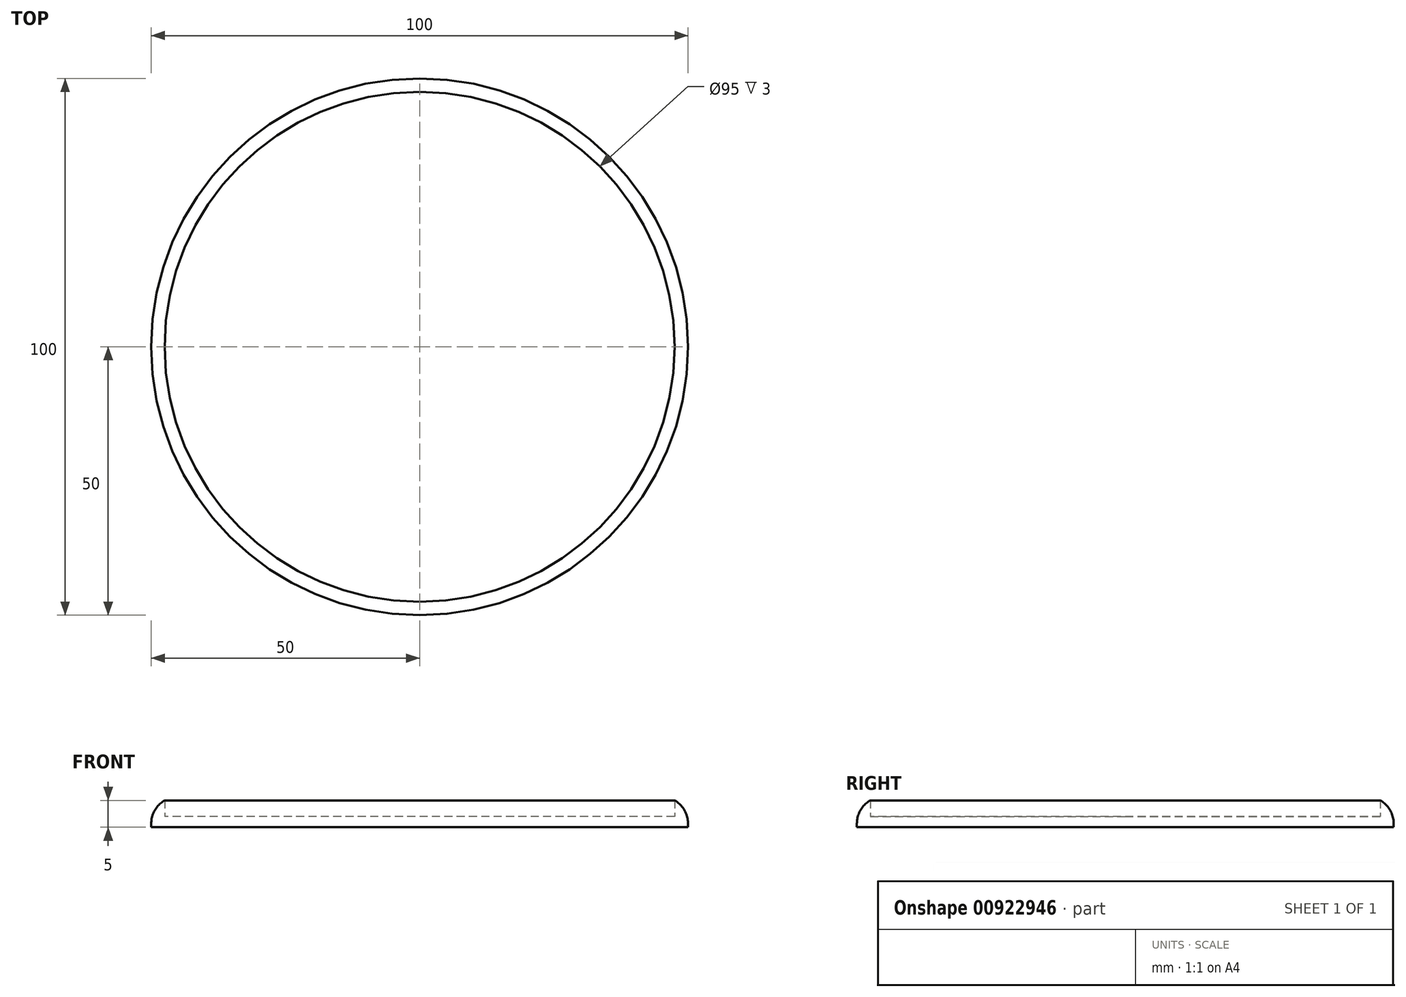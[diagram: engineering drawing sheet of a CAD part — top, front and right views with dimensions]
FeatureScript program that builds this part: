
annotation { "Feature Type Name" : "Feature", "Feature Type Description" : "" }
export const myFeature = defineFeature(function(context is Context, id is Id, definition is map)
    precondition{}
    {
        {
            var Q0;
            Q0=qCreatedBy(makeId("Top.planeOp"),FACE);
            var sketch = newSketch(context, id + "F0", { "sketchPlane" : qUnion([Q0])});
            skCircle(sketch, "E0", {"center": v(0, 0) * mm, "radius": 50 * mm});
            skCircle(sketch, "E1", {"center": v(0, 0) * mm, "radius": 47.5 * mm});
            skSolve(sketch);
        }
        {
            var Q0;
            Q0 = qSketchRegion(id + "F0", true);
            extrude(context, id + "F1", {"entities" : qUnion([Q0]), "depth" : 5 * mm, "offsetDistance" : 25 * mm});
        }
        {
            var Q0;
            Q0=makeQuery(id+"F1.opExtrude","CAP_EDGE",EDGE,{"disambiguationData":[OSD([sQuery(id+"F0.wireOp",EDGE,"E0")])],"isStart":false});
            fillet(context, id + "F2", {"entities" : qUnion([Q0]), "radius" : 5 * mm, "tangentPropagation" : true, "allowEdgeOverflow" : false});
        }
        {
            var Q0;
            Q0=makeQuery(id+"F0.imprint","IMPRINT",FACE,{"disambiguationData":[TD([[makeQuery(id+"F0.imprint","IMPRINT",EDGE,{"derivedFrom":sQuery(id+"F0.wireOp",EDGE,"E1")}),1.0]])]});
            extrude(context, id + "F3", {"entities" : qUnion([Q0]), "operationType" : NewBodyOperationType.ADD, "depth" : 2 * mm, "offsetDistance" : 25 * mm});
        }
    });
